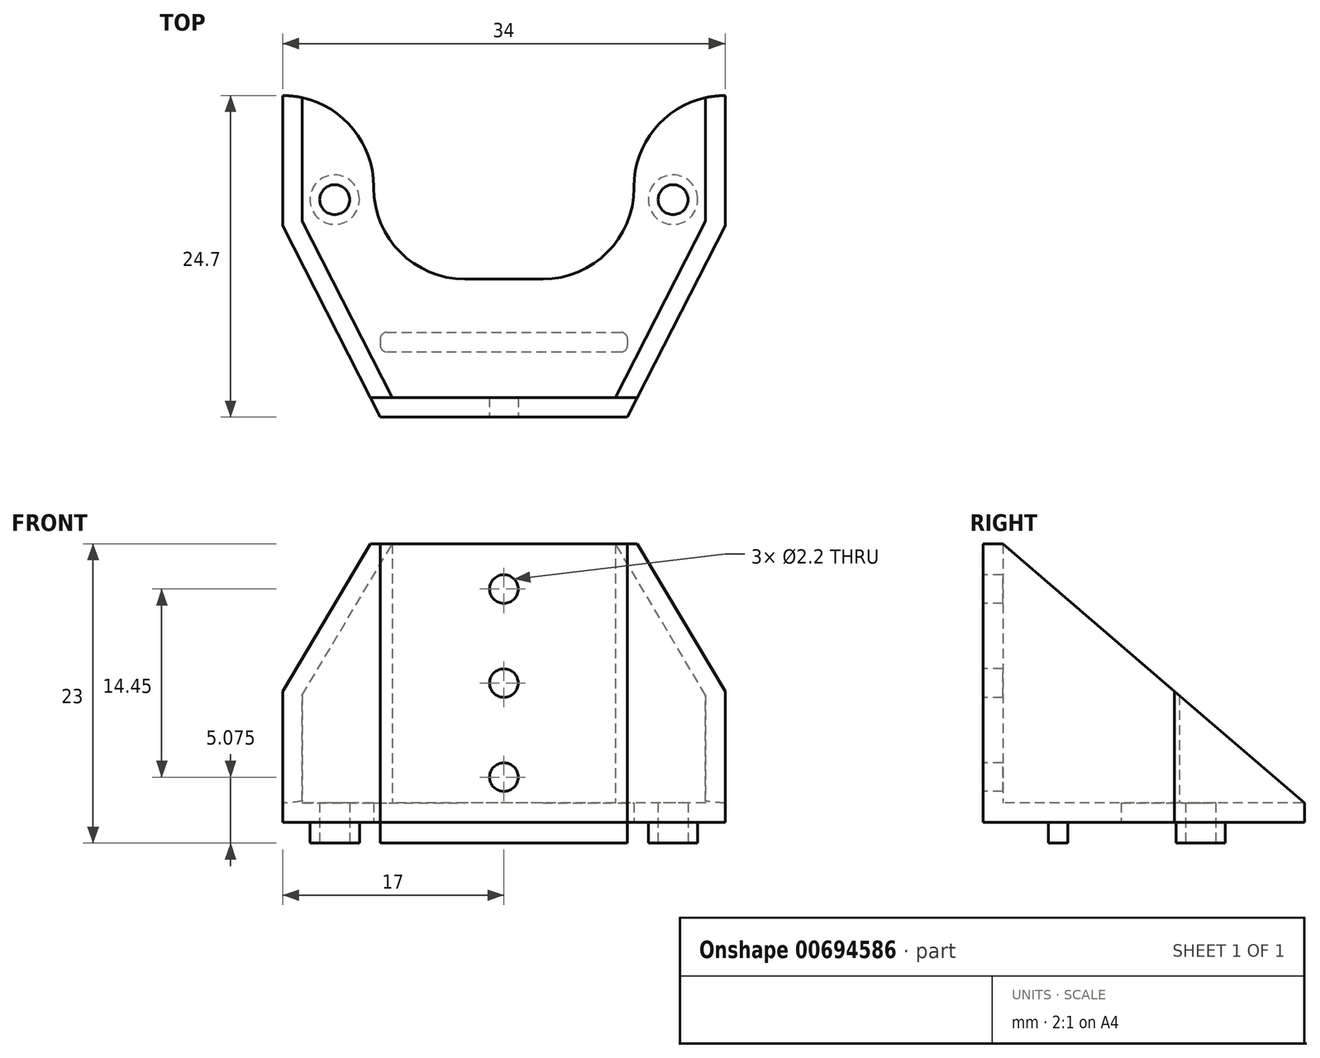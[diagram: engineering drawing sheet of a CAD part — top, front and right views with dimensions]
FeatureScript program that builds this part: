
annotation { "Feature Type Name" : "Feature", "Feature Type Description" : "" }
export const myFeature = defineFeature(function(context is Context, id is Id, definition is map)
    precondition{}
    {
        {
            var Q0;
            Q0=qCreatedBy(makeId("Top.planeOp"),FACE);
            var sketch = newSketch(context, id + "F0", { "sketchPlane" : qUnion([Q0])});
            skLineSegment(sketch, "E0", {"start": v(-15, -8.1) * mm, "end": v(15, -8.1) * mm});
            skLineSegment(sketch, "E1.bottom", {"start": v(-15, 24) * mm, "end": v(-11, 24) * mm});
            skLineSegment(sketch, "E1.top", {"start": v(-15, 0) * mm, "end": v(-11, 0) * mm});
            skLineSegment(sketch, "E1.left", {"start": v(-15, 24) * mm, "end": v(-15, 0) * mm});
            skLineSegment(sketch, "E1.right", {"start": v(-11, 24) * mm, "end": v(-11, 0) * mm});
            skLineSegment(sketch, "E2.MirrorCS", {"start": v(11, 24) * mm, "end": v(11, 0) * mm});
            skLineSegment(sketch, "E3.MirrorCS", {"start": v(15, 24) * mm, "end": v(15, 0) * mm});
            skLineSegment(sketch, "E4.MirrorCS", {"start": v(15, 24) * mm, "end": v(11, 24) * mm});
            skLineSegment(sketch, "E5.MirrorCS", {"start": v(15, 0) * mm, "end": v(11, 0) * mm});
            skSolve(sketch);
        }
        {
            var Q0;
            Q0=qCreatedBy(makeId("Top.planeOp"),FACE);
            var sketch = newSketch(context, id + "F1", { "sketchPlane" : qUnion([Q0])});
            skCircle(sketch, "E6", {"center": v(-13, 2) * mm, "radius": 1.9 * mm});
            skCircle(sketch, "E7.MirrorC", {"center": v(13, 2) * mm, "radius": 1.9 * mm});
            skLineSegment(sketch, "E8.bottom", {"start": v(-9.5, -8.2) * mm, "end": v(9.5, -8.2) * mm});
            skLineSegment(sketch, "E8.top", {"start": v(-9.5, -9.7) * mm, "end": v(9.5, -9.7) * mm});
            skLineSegment(sketch, "E8.left", {"start": v(-9.5, -8.2) * mm, "end": v(-9.5, -9.7) * mm});
            skLineSegment(sketch, "E8.right", {"start": v(9.5, -8.2) * mm, "end": v(9.5, -9.7) * mm});
            skSolve(sketch);
        }
        {
            var Q0;
            Q0=qCreatedBy(makeId("Top.planeOp"),FACE);
            var sketch = newSketch(context, id + "F2", { "sketchPlane" : qUnion([Q0])});
            skLineSegment(sketch, "E9", {"start": v(-9.5, -14.7) * mm, "end": v(-17, 0) * mm});
            skLineSegment(sketch, "E10", {"start": v(-17, 0) * mm, "end": v(-17, 10) * mm});
            skLineSegment(sketch, "E11", {"start": v(-17, 10) * mm, "end": v(-10, 10) * mm});
            skLineSegment(sketch, "E12", {"start": v(-10, 10) * mm, "end": v(-10, -4.1) * mm});
            skLineSegment(sketch, "E13", {"start": v(-10, -4.1) * mm, "end": v(0, -4.1) * mm});
            skLineSegment(sketch, "E14", {"start": v(-9.5, -14.7) * mm, "end": v(0, -14.7) * mm});
            skLineSegment(sketch, "E15.MirrorCS", {"start": v(10, -4.1) * mm, "end": v(0, -4.1) * mm});
            skLineSegment(sketch, "E16.MirrorCS", {"start": v(10, 10) * mm, "end": v(10, -4.1) * mm});
            skLineSegment(sketch, "E17.MirrorCS", {"start": v(17, 10) * mm, "end": v(10, 10) * mm});
            skLineSegment(sketch, "E18.MirrorCS", {"start": v(17, 0) * mm, "end": v(17, 10) * mm});
            skLineSegment(sketch, "E19.MirrorCS", {"start": v(9.5, -14.7) * mm, "end": v(17, 0) * mm});
            skLineSegment(sketch, "E20.MirrorCS", {"start": v(9.5, -14.7) * mm, "end": v(0, -14.7) * mm});
            skSolve(sketch);
        }
        {
            var Q0;
            Q0=makeQuery(id+"F2.imprint","IMPRINT",FACE,{"disambiguationData":[TD([[makeQuery(id+"F2.imprint","IMPRINT",EDGE,{"derivedFrom":sQuery(id+"F2.wireOp",EDGE,"E9")}),-1.0]])]});
            var sketch = newSketch(context, id + "F3", { "sketchPlane" : qUnion([Q0])});
            skLineSegment(sketch, "E21", {"start": v(-17, 10) * mm, "end": v(-17, 0) * mm});
            skLineSegment(sketch, "E22", {"start": v(-17, 0) * mm, "end": v(-9.5, -14.7) * mm});
            skLineSegment(sketch, "E23", {"start": v(-9.5, -14.7) * mm, "end": v(0, -14.7) * mm});
            skLineSegment(sketch, "E24", {"start": v(-17, 10) * mm, "end": v(-15.5, 10) * mm});
            skLineSegment(sketch, "E25", {"start": v(-15.5, 10) * mm, "end": v(-15.5, 0.36) * mm});
            skLineSegment(sketch, "E26", {"start": v(-15.5, 0.36) * mm, "end": v(-8.58, -13.2) * mm});
            skLineSegment(sketch, "E27", {"start": v(-8.58, -13.2) * mm, "end": v(0, -13.2) * mm});
            skPoint(sketch, "E28.orphan", {"position": v(-15.5, 0) * mm});
            skLineSegment(sketch, "E29.MirrorCS", {"start": v(15.5, 10) * mm, "end": v(15.5, 0.36) * mm});
            skLineSegment(sketch, "E30.MirrorCS", {"start": v(17, 10) * mm, "end": v(17, 0) * mm});
            skLineSegment(sketch, "E31.MirrorCS", {"start": v(17, 0) * mm, "end": v(9.5, -14.7) * mm});
            skLineSegment(sketch, "E32.MirrorCS", {"start": v(9.5, -14.7) * mm, "end": v(0, -14.7) * mm});
            skLineSegment(sketch, "E33.MirrorCS", {"start": v(8.58, -13.2) * mm, "end": v(0, -13.2) * mm});
            skLineSegment(sketch, "E34.MirrorCS", {"start": v(15.5, 0.36) * mm, "end": v(8.58, -13.2) * mm});
            skLineSegment(sketch, "E35.MirrorCS", {"start": v(17, 10) * mm, "end": v(15.5, 10) * mm});
            skSolve(sketch);
        }
        {
            var Q0;
            Q0 = qSketchRegion(id + "F3", true);
            extrude(context, id + "F4", {"entities" : qUnion([Q0]), "depth" : 21.4 * mm, "offsetDistance" : 25 * mm});
        }
        {
            var Q0;
            Q0 = qSketchRegion(id + "F2", true);
            extrude(context, id + "F5", {"entities" : qUnion([Q0]), "operationType" : NewBodyOperationType.ADD, "depth" : 1.5 * mm, "offsetDistance" : 25 * mm});
        }
        {
            var Q0;
            Q0 = qSketchRegion(id + "F1", true);
            extrude(context, id + "F6", {"entities" : qUnion([Q0]), "operationType" : NewBodyOperationType.ADD, "oppositeDirection" : true, "depth" : 1.6 * mm, "offsetDistance" : 25 * mm});
        }
        {
            var Q0;
            Q0=qCreatedBy(makeId("Right.planeOp"),FACE);
            var sketch = newSketch(context, id + "F7", { "sketchPlane" : qUnion([Q0])});
            skLineSegment(sketch, "E36", {"start": v(10, 1.5) * mm, "end": v(-13.2, 21.4) * mm});
            skLineSegment(sketch, "E37", {"start": v(-13.2, 21.4) * mm, "end": v(10, 21.4) * mm});
            skLineSegment(sketch, "E38", {"start": v(10, 21.4) * mm, "end": v(10, 1.5) * mm});
            skSolve(sketch);
        }
        {
            var Q0;
            Q0 = qSketchRegion(id + "F7", true);
            extrude(context, id + "F8", {"entities" : qUnion([Q0]), "operationType" : NewBodyOperationType.REMOVE, "endBound" : BoundingType.THROUGH_ALL, "oppositeDirection" : true, "depth" : 25 * mm, "offsetDistance" : 25 * mm, "hasSecondDirection" : true, "secondDirectionBound" : SecondDirectionBoundingType.THROUGH_ALL, "secondDirectionOppositeDirection" : false, "secondDirectionDepth" : 25 * mm});
        }
        {
            var Q0;
            Q0=qCreatedBy(makeId("Top.planeOp"),FACE);
            var sketch = newSketch(context, id + "F9", { "sketchPlane" : qUnion([Q0])});
            skCircle(sketch, "E39", {"center": v(13, 2) * mm, "radius": 1.15 * mm});
            skCircle(sketch, "E40.MirrorC", {"center": v(-13, 2) * mm, "radius": 1.15 * mm});
            skSolve(sketch);
        }
        {
            var Q0;
            Q0 = qSketchRegion(id + "F9", true);
            extrude(context, id + "F10", {"entities" : qUnion([Q0]), "operationType" : NewBodyOperationType.REMOVE, "endBound" : BoundingType.THROUGH_ALL, "depth" : 25 * mm, "offsetDistance" : 25 * mm, "hasSecondDirection" : true, "secondDirectionBound" : SecondDirectionBoundingType.THROUGH_ALL, "secondDirectionOppositeDirection" : true, "secondDirectionDepth" : 25 * mm});
        }
        {
            var Q0;
            Q0=makeQuery(id+"F4.opExtrude","SWEPT_FACE",FACE,{"disambiguationData":[OSD([sQuery(id+"F3.wireOp",EDGE,"E23"),sQuery(id+"F3.wireOp",EDGE,"E32.MirrorCS")])]});
            var sketch = newSketch(context, id + "F11", { "sketchPlane" : qUnion([Q0])});
            skCircle(sketch, "E41", {"center": v(0, 3.47) * mm, "radius": 1.1 * mm});
            skCircle(sketch, "E42", {"center": v(0, 17.92) * mm, "radius": 1.1 * mm});
            skCircle(sketch, "E43", {"center": v(0, 10.7) * mm, "radius": 1.1 * mm});
            skSolve(sketch);
        }
        {
            var Q0;
            Q0 = qSketchRegion(id + "F11", true);
            extrude(context, id + "F12", {"entities" : qUnion([Q0]), "operationType" : NewBodyOperationType.REMOVE, "endBound" : BoundingType.UP_TO_NEXT, "oppositeDirection" : true, "depth" : 25 * mm, "offsetDistance" : 25 * mm});
        }
        {
            var Q0;
            Q0=makeQuery(id+"F5.opExtrude","SWEPT_EDGE",EDGE,{"disambiguationData":[OSD([sQuery(id+"F2.wireOp",EDGE,"E11"),sQuery(id+"F2.wireOp",EDGE,"E12")])]});
            var Q1;
            Q1=makeQuery(id+"F5.opExtrude","SWEPT_EDGE",EDGE,{"disambiguationData":[OSD([sQuery(id+"F2.wireOp",EDGE,"E16.MirrorCS"),sQuery(id+"F2.wireOp",EDGE,"E17.MirrorCS")])]});
            var Q2;
            Q2=makeQuery(id+"F5.opExtrude","SWEPT_EDGE",EDGE,{"disambiguationData":[OSD([sQuery(id+"F2.wireOp",EDGE,"E15.MirrorCS"),sQuery(id+"F2.wireOp",EDGE,"E16.MirrorCS")])]});
            var Q3;
            Q3=makeQuery(id+"F5.opExtrude","SWEPT_EDGE",EDGE,{"disambiguationData":[OSD([sQuery(id+"F2.wireOp",EDGE,"E12"),sQuery(id+"F2.wireOp",EDGE,"E13")])]});
            fillet(context, id + "F13", {"entities" : qUnion([Q0, Q1, Q2, Q3]), "radius" : 7 * mm, "tangentPropagation" : true, "allowEdgeOverflow" : false});
        }
        {
            var Q0;
            Q0=makeQuery(id+"F6.opExtrude","SWEPT_EDGE",EDGE,{"disambiguationData":[OSD([sQuery(id+"F1.wireOp",EDGE,"E8.bottom"),sQuery(id+"F1.wireOp",EDGE,"E8.left")])]});
            var Q1;
            Q1=makeQuery(id+"F6.opExtrude","SWEPT_EDGE",EDGE,{"disambiguationData":[OSD([sQuery(id+"F1.wireOp",EDGE,"E8.top"),sQuery(id+"F1.wireOp",EDGE,"E8.left")])]});
            var Q2;
            Q2=makeQuery(id+"F6.opExtrude","SWEPT_EDGE",EDGE,{"disambiguationData":[OSD([sQuery(id+"F1.wireOp",EDGE,"E8.bottom"),sQuery(id+"F1.wireOp",EDGE,"E8.right")])]});
            var Q3;
            Q3=makeQuery(id+"F6.opExtrude","SWEPT_EDGE",EDGE,{"disambiguationData":[OSD([sQuery(id+"F1.wireOp",EDGE,"E8.top"),sQuery(id+"F1.wireOp",EDGE,"E8.right")])]});
            fillet(context, id + "F14", {"entities" : qUnion([Q0, Q1, Q2, Q3]), "radius" : 0.5 * mm, "tangentPropagation" : true, "allowEdgeOverflow" : false});
        }
    });
